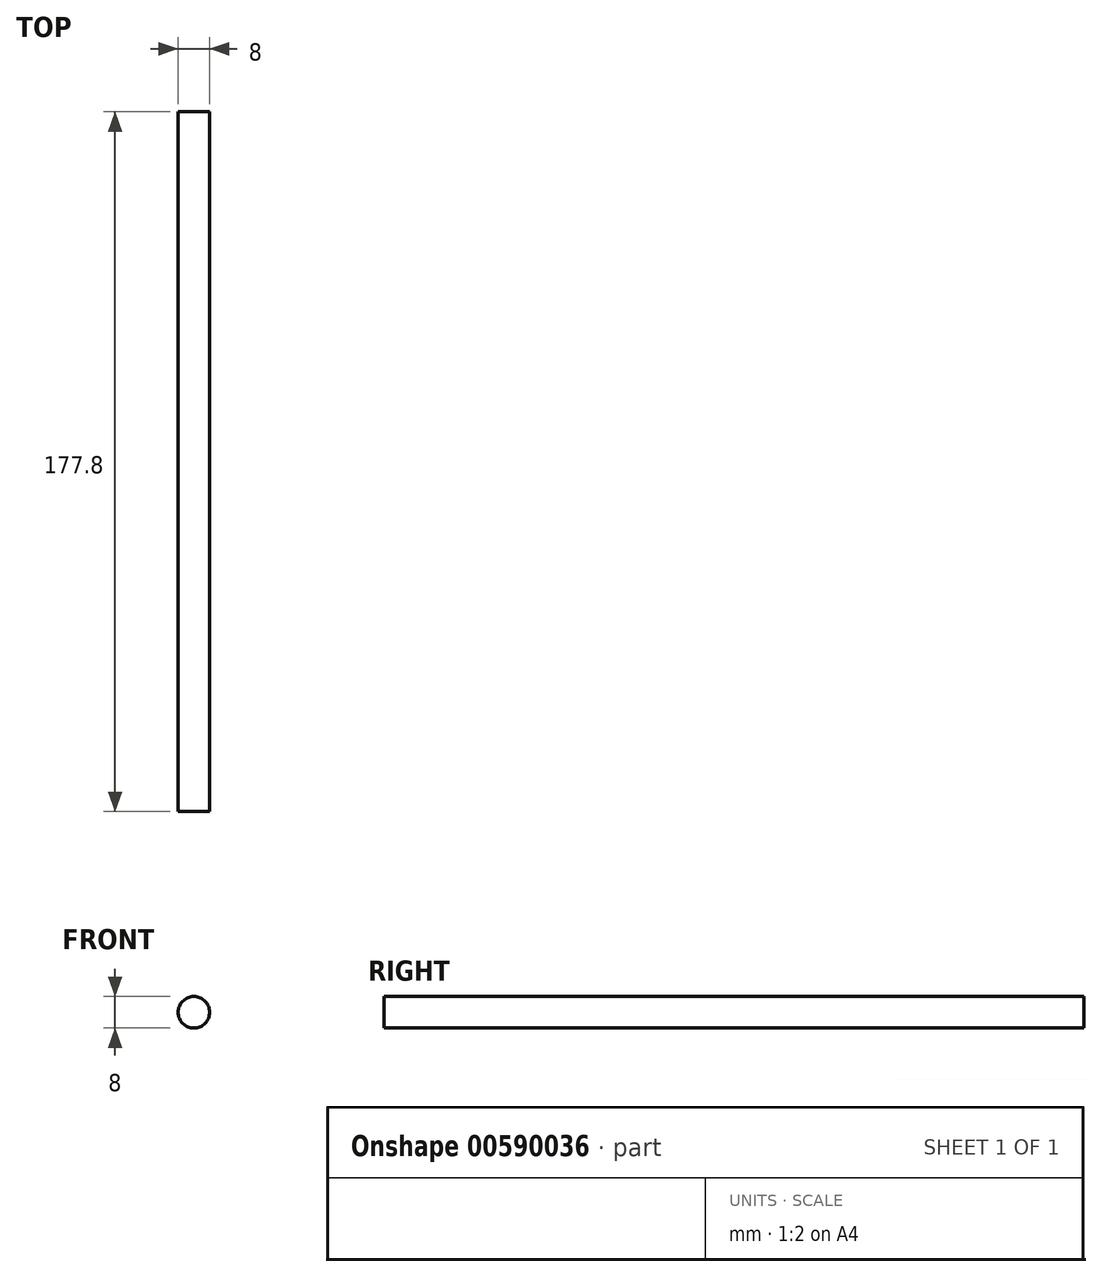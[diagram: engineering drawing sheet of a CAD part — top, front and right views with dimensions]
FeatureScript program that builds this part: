
annotation { "Feature Type Name" : "Feature", "Feature Type Description" : "" }
export const myFeature = defineFeature(function(context is Context, id is Id, definition is map)
    precondition{}
    {
        {
            var Q0;
            Q0=qCreatedBy(makeId("Front.planeOp"),FACE);
            var sketch = newSketch(context, id + "F0", { "sketchPlane" : qUnion([Q0])});
            skCircle(sketch, "E0", {"center": v(0, 0) * mm, "radius": 4 * mm});
            skSolve(sketch);
        }
        {
            var Q0;
            Q0=makeQuery(id+"F0.imprint","IMPRINT",FACE,{"disambiguationData":[TD([[makeQuery(id+"F0.imprint","IMPRINT",EDGE,{"derivedFrom":sQuery(id+"F0.wireOp",EDGE,"E0")}),1.0]])]});
            extrude(context, id + "F1", {"entities" : qUnion([Q0]), "endBound" : BoundingType.SYMMETRIC, "depth" : 177.8 * mm, "offsetDistance" : 25.4 * mm});
        }
    });
